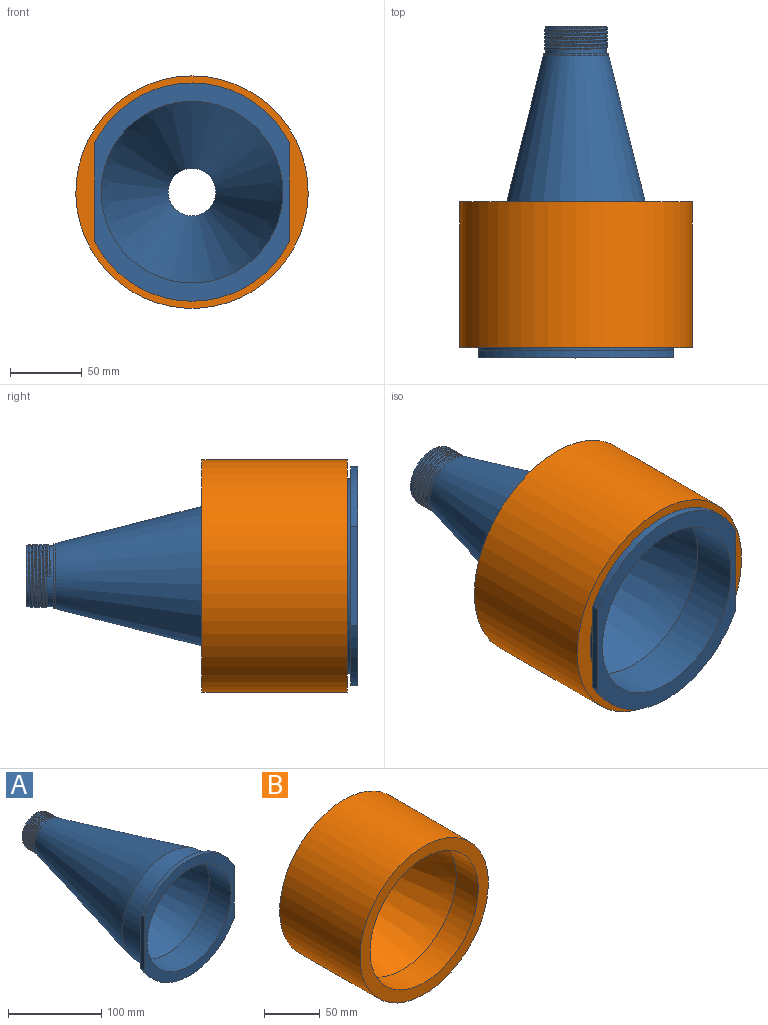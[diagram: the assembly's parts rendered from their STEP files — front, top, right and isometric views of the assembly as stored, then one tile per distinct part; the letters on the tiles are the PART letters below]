
ASSEMBLY  parts=2 mates=1
PART A: 25 faces, bbox 136x231.7x152.5 mm
  f0: cylinder r=21.34mm len=42.67mm, axis (0,-1,0), area 497.6mm2, adj f4,f13,f21,f23,f24
  f1: cylinder r=21.34mm len=42.67mm, axis (0,-1,0), area 276.2mm2, adj f2,f19,f20,f23,f24
  f2: cylinder r=21.34mm len=42.67mm, axis (0,-1,0), area 30.3mm2, adj f1,f3,f23,f24
  f3: cylinder r=21.34mm len=42.67mm, axis (0,-1,0), area 30.3mm2, adj f2,f4,f23,f24
  f4: cylinder r=21.34mm len=42.67mm, axis (0,-1,0), area 30.3mm2, adj f0,f3,f23,f24
  f5: plane 135.89x76.2mm, normal (0,1,0), area 1485.1mm2, adj f8,f15,f17,f18
  f6: plane 135.89x76.2mm, normal (0,1,0), area 1485.1mm2, adj f15,f16,f17,f18
  f7: plane 152.4x135.89mm, normal (0,-1,0), area 4805.8mm2, adj f8,f14,f16,f17,f18
  f8: cylinder r=76.2mm len=135.89mm, axis (0,1,0), area 852.4mm2, adj f5,f7,f17,f18
  f9: cone r=22.78mm half-angle=14.2deg, axis (0,-1,0), area 52386.3mm2, adj f12,f15
  f10: cone r=63.5mm half-angle=14.7deg, axis (0,-1,0), area 46377.8mm2, adj f11,f14
  f11: cylinder r=16.64mm len=33.27mm, axis (0,-1,0), area 2140mm2, adj f10,f19
  f12: cylinder r=22.78mm len=45.57mm, axis (0,-1,0), area 185.4mm2, adj f9,f13
  f13: plane 45.57x45.57mm, normal (0,1,0), area 200.7mm2, adj f0,f12
  f14: cylinder r=63.5mm len=127mm, axis (0,1,0), area 13174.4mm2, adj f7,f10
  f15: cylinder r=67.95mm len=135.89mm, axis (0,1,0), area 11927.9mm2, adj f5,f6,f9
  f16: cylinder r=76.2mm len=135.89mm, axis (0,1,0), area 852.4mm2, adj f6,f7,f17,f18
  f17: plane 68.99x5.08mm, normal (-1,0,0), area 350.5mm2, adj f5,f6,f7,f8,f16
  f18: plane 68.99x5.08mm, normal (1,0,0), area 350.5mm2, adj f5,f6,f7,f8,f16
  f19: plane 42.67x42.67mm, normal (0,1,0), area 560.6mm2, adj f1,f11
  f20: plane 2.39x0.82mm, normal (0,0,-1), area 0.9mm2, adj f1,f22,f23,f24
  f21: plane 2.39x0.82mm, normal (0,0,-1), area 0.9mm2, adj f0,f22,f23,f24
  f22: bspline ~52.65x45.59mm, area 1321.2mm2, adj f20,f21,f23,f24
  f23: bspline ~43.29x43.29mm, area 431.1mm2, adj f0,f1,f2,f3,f4,f20,f21,f22
  f24: bspline ~43.29x43.29mm, area 431mm2, adj f0,f1,f2,f3,f4,f20,f21,f22
PART B: 6 faces, bbox 162.3x101.6x162.3 mm
  f0: cylinder r=50.42mm len=100.84mm, axis (0,1,0), area 2333.5mm2, adj f1,f5
  f1: plane 162.26x162.26mm, normal (0,1,0), area 12690.8mm2, adj f0,f2
  f2: cylinder r=81.13mm len=162.26mm, axis (0,1,0), area 51789.6mm2, adj f1,f3
  f3: plane 162.26x162.26mm, normal (0,-1,0), area 5967mm2, adj f2,f4
  f4: cylinder r=68.43mm len=136.86mm, axis (0,1,0), area 12012.6mm2, adj f3,f5
  f5: cone r=68.43mm half-angle=15.2deg, axis (0,-1,0), area 25649mm2, adj f0,f4
PLACE A t=(0,104.5,-1.09)mm
PLACE B t=(0,2.17,-1.09)mm
MATE slider A.f15 <-> B.f0  axis (0,1,0) through (0,-87.63,-1.09)mm
